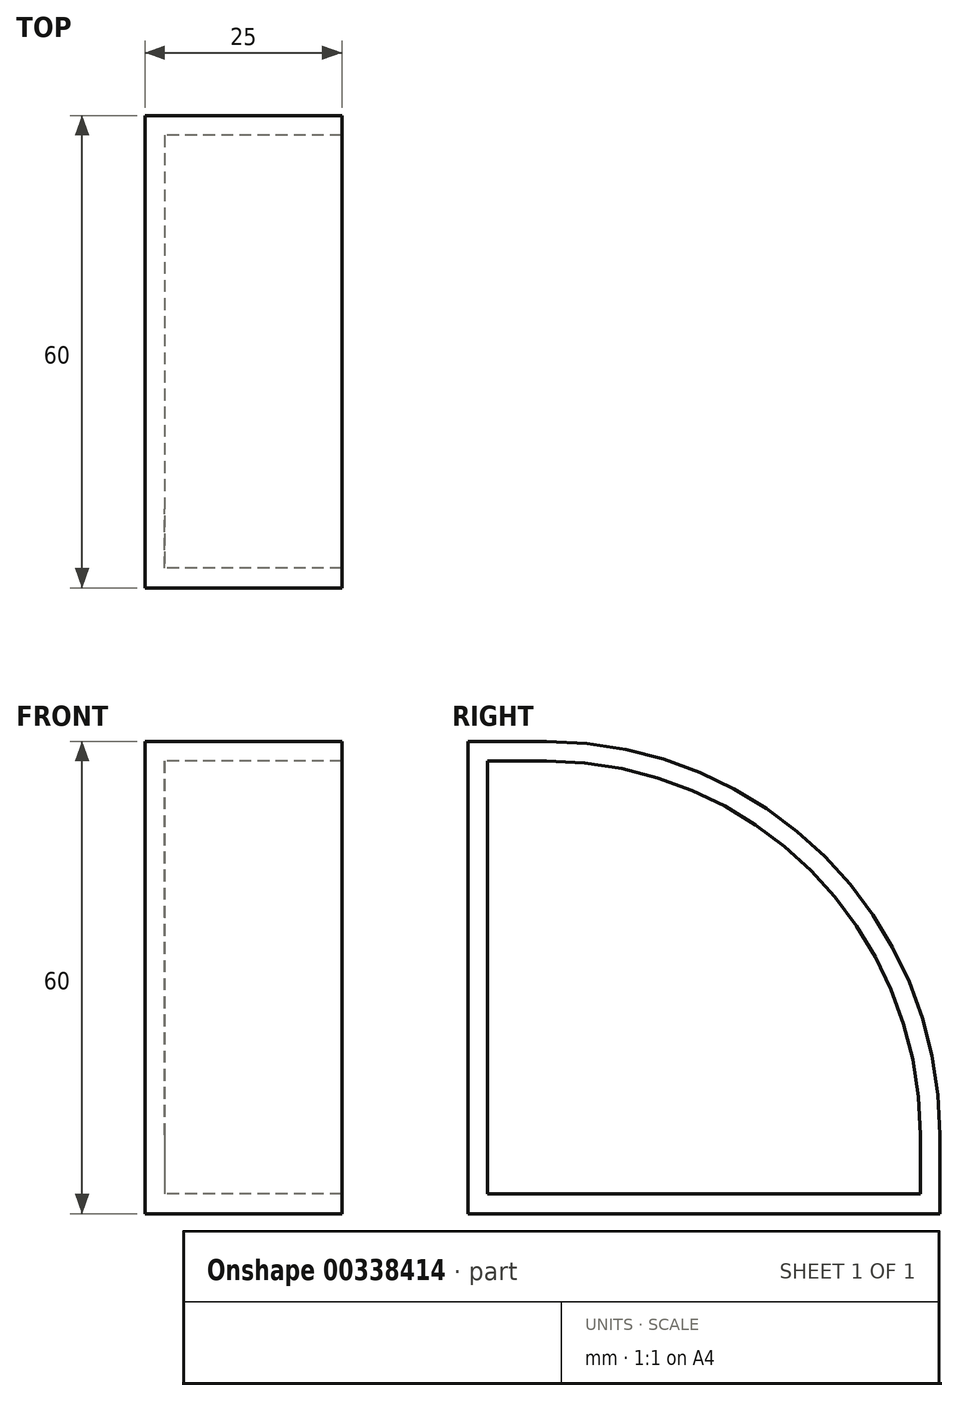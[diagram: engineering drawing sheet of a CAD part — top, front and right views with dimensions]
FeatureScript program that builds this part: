
annotation { "Feature Type Name" : "Feature", "Feature Type Description" : "" }
export const myFeature = defineFeature(function(context is Context, id is Id, definition is map)
    precondition{}
    {
        {
            var Q0;
            Q0=qCreatedBy(makeId("Right.planeOp"),FACE);
            var sketch = newSketch(context, id + "F0", { "sketchPlane" : qUnion([Q0])});
            skLineSegment(sketch, "E0", {"start": v(0, 34.03) * mm, "end": v(0, -25.97) * mm});
            skLineSegment(sketch, "E1", {"start": v(0, 34.03) * mm, "end": v(60, 34.03) * mm});
            skLineSegment(sketch, "E2", {"start": v(60, 34.03) * mm, "end": v(60, -25.97) * mm});
            skLineSegment(sketch, "E3", {"start": v(60, -25.97) * mm, "end": v(0, -25.97) * mm});
            skSolve(sketch);
        }
        {
            var Q0;
            Q0=makeQuery(id+"F0.imprint","IMPRINT",FACE,{"disambiguationData":[TD([[makeQuery(id+"F0.imprint","IMPRINT",EDGE,{"derivedFrom":sQuery(id+"F0.wireOp",EDGE,"E0")}),1.0]])]});
            extrude(context, id + "F1", {"entities" : qUnion([Q0]), "depth" : 25 * mm});
        }
        {
            var Q0;
            Q0=makeQuery(id+"F1.opExtrude","SWEPT_EDGE",EDGE,{"disambiguationData":[OSD([sQuery(id+"F0.wireOp",EDGE,"E1"),sQuery(id+"F0.wireOp",EDGE,"E2")])]});
            fillet(context, id + "F2", {"entities" : qUnion([Q0]), "radius" : 50 * mm, "tangentPropagation" : true, "allowEdgeOverflow" : false});
        }
        {
            var Q0;
            Q0=makeQuery(id+"F1.opExtrude","CAP_FACE",FACE,{"disambiguationData":[OSD([sQuery(id+"F0.wireOp",EDGE,"E0"),sQuery(id+"F0.wireOp",EDGE,"E1"),sQuery(id+"F0.wireOp",EDGE,"E2"),sQuery(id+"F0.wireOp",EDGE,"E3")])],"isStart":false});
            shell(context, id + "F3", {"entities" : qUnion([Q0]), "thickness" : 2.5 * mm});
        }
    });
